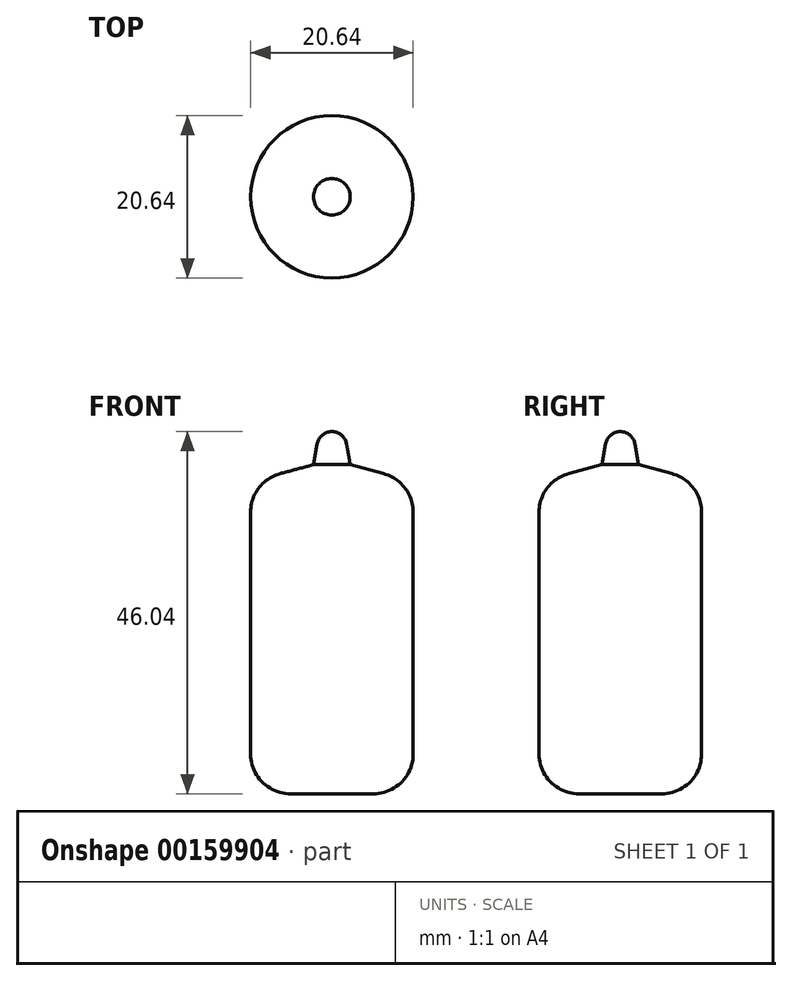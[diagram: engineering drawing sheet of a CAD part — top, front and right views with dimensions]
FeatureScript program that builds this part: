
annotation { "Feature Type Name" : "Feature", "Feature Type Description" : "" }
export const myFeature = defineFeature(function(context is Context, id is Id, definition is map)
    precondition{}
    {
        {
            var Q0;
            Q0=qCreatedBy(makeId("Top.planeOp"),FACE);
            var sketch = newSketch(context, id + "F0", { "sketchPlane" : qUnion([Q0])});
            skCircle(sketch, "E0", {"center": v(0, 0) * mm, "radius": 10.32 * mm});
            skSolve(sketch);
        }
        {
            var Q0;
            Q0=qCreatedBy(makeId("Front.planeOp"),FACE);
            var sketch = newSketch(context, id + "F1", { "sketchPlane" : qUnion([Q0])});
            skLineSegment(sketch, "E1", {"start": v(10.32, 0) * mm, "end": v(10.32, 39.69) * mm});
            skLineSegment(sketch, "E2", {"start": v(10.32, 39.69) * mm, "end": v(0, 39.69) * mm, "construction": true});
            skLineSegment(sketch, "E3", {"start": v(0, 39.69) * mm, "end": v(0, 46.04) * mm, "construction": true});
            skLineSegment(sketch, "E4", {"start": v(0, 46.04) * mm, "end": v(1.59, 46.04) * mm, "construction": true});
            skLineSegment(sketch, "E5", {"start": v(1.86, 44.47) * mm, "end": v(2.33, 41.83) * mm});
            skLineSegment(sketch, "E6", {"start": v(2.33, 41.83) * mm, "end": v(10.32, 39.69) * mm});
            skArc(sketch, "E7", {"start": v(1.86, 44.47) * mm, "mid": v(1.22, 45.6) * mm, "end": v(0, 46.04) * mm});
            skLineSegment(sketch, "E8", {"start": v(0, 46.04) * mm, "end": v(0, 0) * mm});
            skLineSegment(sketch, "E9", {"start": v(0, 0) * mm, "end": v(10.32, 0) * mm});
            skSolve(sketch);
        }
        {
            var Q0;
            Q0=makeQuery(id+"F1.imprint","IMPRINT",FACE,{"disambiguationData":[TD([[makeQuery(id+"F1.imprint","IMPRINT",EDGE,{"derivedFrom":sQuery(id+"F1.wireOp",EDGE,"E1")}),1.0]])]});
            var Q1;
            Q1=sQuery(id+"F1.wireOp",EDGE,"E8");
            revolve(context, id + "F2", {"entities" : qUnion([Q0]), "axis" : qUnion([Q1]), "revolveType" : RevolveType.FULL});
        }
        {
            var Q0;
            Q0=makeQuery(id+"F2.opRevolve","SWEPT_EDGE",EDGE,{"disambiguationData":[OSD([sQuery(id+"F1.wireOp",EDGE,"E1"),sQuery(id+"F1.wireOp",EDGE,"E6")])]});
            var Q1;
            Q1=makeQuery(id+"F2.opRevolve","SWEPT_EDGE",EDGE,{"disambiguationData":[OSD([sQuery(id+"F1.wireOp",EDGE,"E1"),sQuery(id+"F1.wireOp",EDGE,"E9")])]});
            fillet(context, id + "F3", {"entities" : qUnion([Q0, Q1]), "radius" : 5.08 * mm, "tangentPropagation" : true, "allowEdgeOverflow" : false});
        }
    });
